# Revit family: RN 55023 Optipress-Therm-Längenkompensator
name_source: partatom
category: Rohrformteile
units: mm (PartAtom-declared; Revit-internal decimal feet)

## family parameters
Arbeitsebenenbasiert = Nein
Beim Laden mit Abzugskörper schneiden = Nein
Bemaßung runder Anschluss = Durchmesser verwenden
Gemeinsam genutzt = Nein
Immer vertikal = Ja
Teiletyp = Nicht definiert

## types (5) — shared parameters
1.010.00.2 Blattnummer der Richtlinie = 29
1.010.00.3 Ausgabedatum (Monat) der Richtlinie = 201308
1.010.00.4 Herstellername = R. Nussbaum AG
1.010.00.5 Revisionsdatum der Datei = 20190521
1.010.00.6 Webadresse des Herstellers = http://www.nussbaum.ch
1.100.00.4 Produktbezeichnung = Versorgung
1.110.00.2 Index = 1
1.110.00.4 Produktbezeichnung = Optipress-Therm
1.960/3L.00.8 Link (URL) = https://www.nussbaum.ch
29.700.00.4 Produktname = Optipress-Therm-Längenkompensator, vorgespannt
29.700.00.5 Produktkennung = 2
29.700.00.6 Querschnittsform = 1
29.700.00.7 Nennweitensystem = DN
29.700.00.8 Nenndrucksystem = PN
29.710.02.4 Nenndruck = 16
29.710.02.5 max. zul. Überdruck [hPa] = 1600
29.710.02.7 max. zul. Dauer-Betriebsdruck [hPa] = 1600
29.710.02.9 max. zul. Dauer-Betriebstemperatur [°C] = 90
Connector Visibility = Nein
EnclosingSpace Visibility = Nein
Hersteller = R. Nussbaum AG

## per-type parameters (varying)
| type | 1.800.00.3 TGA-Nummer | 1.800.00.4 Kommentarfeld | 1.810.00.3 Hersteller-Bestellnummer | 1.810.00.4 DATANORM-Nummer | 1.810.00.6 GTIN-Nummer | 29.710.02.10 Formstück-Gewicht [kg] | 29.710.02.3 Benennung | CONNECTOR0_DIAMETER_dX_0r | CONNECTOR0_dX_01 | CONNECTOR0_ref_dX | CONNECTOR1_DIAMETER_dX_0r | CONNECTOR1_dX_00 | CONNECTOR1_dX_01 | CONNECTOR1_ref_dX | Modell | R. Nussbaum AG 55023.34 de Visibility | R. Nussbaum AG 55023.35 de Visibility | R. Nussbaum AG 55023.36 de Visibility | R. Nussbaum AG 55023.37 de Visibility | R. Nussbaum AG 55023.38 de Visibility | Typenkommentare |
| DN=50 | 01900100000000000000000000000000000000000000000015000000000000000007 | 55023.38, Optipress-Therm-Längenkompensator, vorgespannt, DN=50, L=360 | 55023.38 | 55023.38 | 7612945741127 | 2.359 | Optipress-Therm-Längenkompensator, vorgespannt, DN=50, L=360 | 50 mm | 40 mm | 40 mm | 50 mm | 310 mm | 350 mm | 310 mm | 55023.38 | Nein | Nein | Nein | Nein | Ja | Optipress-Therm-Längenkompensator DN=50 |
| DN=40 | 01900100000000000000000000000000000000000000000015000000000000000006 | 55023.37, Optipress-Therm-Längenkompensator, vorgespannt, DN=40, L=350 | 55023.37 | 55023.37 | 7612945741110 | 1.661 | Optipress-Therm-Längenkompensator, vorgespannt, DN=40, L=350 | 40 mm | 36 mm | 36 mm | 40 mm | 296 mm | 332 mm | 296 mm | 55023.37 | Nein | Nein | Nein | Ja | Nein | Optipress-Therm-Längenkompensator DN=40 |
| DN=32 | 01900100000000000000000000000000000000000000000015000000000000000005 | 55023.36, Optipress-Therm-Längenkompensator, vorgespannt, DN=32, L=316 | 55023.36 | 55023.36 | 7612945741103 | 1.609 | Optipress-Therm-Längenkompensator, vorgespannt, DN=32, L=316 | 32 mm | 26 mm | 26 mm | 32 mm | 284 mm | 310 mm | 284 mm | 55023.36 | Nein | Nein | Ja | Nein | Nein | Optipress-Therm-Längenkompensator DN=32 |
| DN=25 | 01900100000000000000000000000000000000000000000015000000000000000004 | 55023.35, Optipress-Therm-Längenkompensator, vorgespannt, DN=25, L=325 | 55023.35 | 55023.35 | 7612945741097 | 1.149 | Optipress-Therm-Längenkompensator, vorgespannt, DN=25, L=325 | 25 mm  [stored 0.082021 ft] | 24 mm | 24 mm | 25 mm  [stored 0.082021 ft] | 301 mm | 325 mm | 301 mm | 55023.35 | Nein | Ja | Nein | Nein | Nein | Optipress-Therm-Längenkompensator DN=25 |
| DN=20 | 01900100000000000000000000000000000000000000000015000000000000000003 | 55023.34, Optipress-Therm-Längenkompensator, vorgespannt, DN=20, L=325 | 55023.34 | 55023.34 | 7612945741080 | 0.585 | Optipress-Therm-Längenkompensator, vorgespannt, DN=20, L=325 | 20 mm | 24 mm | 24 mm | 20 mm | 291 mm | 315 mm | 291 mm | 55023.34 | Ja | Nein | Nein | Nein | Nein | Optipress-Therm-Längenkompensator DN=20 |

note: [stored X ft] marks values corroborated as IEEE doubles in the binary element streams (Revit-internal decimal feet)

## geometry (parser evidence)
native form markers: Sweep x1
no freeform markers — native parametric forms only
